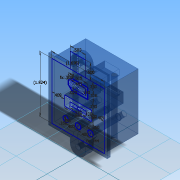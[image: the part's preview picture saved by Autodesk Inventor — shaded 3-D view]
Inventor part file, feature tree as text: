
AUTODESK INVENTOR PART (.ipt)
format: ipt  version: 2014 SP2 (Build 180246200, 246)  size: 236,544 bytes
history: native  units: in
note: dims shown in document units (in); Inventor stores cm internally (conversion verified against a paired STEP export)
features: extrude x10, sketch x4, hole x2, fillet x2, mirror x2, plane x1, projected_geometry x1
ambient origin geometry x8: Origin, YZ Plane, XZ Plane, XY Plane, X Axis, Y Axis, Z Axis, Center Point
bodies: Solid1 (feature_tree)
feature tree (22):
  sketch  "Sketch1"  dims[d1=0.316in d6=0.465in d7=0.19in]
  extrude  "Base"  Depth=0.465in
  extrude  "Flange"  Depth=0.25in
  sketch  "Sketch4"  dims[d19=0.4088in d20=0.4088in d21=1.1in d22=0.0in d23=0.91in d24=0.0in d25=0.16in d26=0.81in d27=0.0in d28=1.03in d29=0.0in d30=1.03in d31=0.0in d32=0.724in d33=0.0in d34=1.03in d35=0.0in d36=0.605in d37=0.25in d38=0.25in d39=0.1in d40=0.1in d42=0.02in d43=0.418in d44=0.0in d45=0.55in d46=0.63in d47=0.15in d48=0.75in d49=0.279in d50=0.25in d51=0.5635in d52=1.0in d53=0.8108in d54=0.1in d55=0.1in d56=0.0in d57=0.5in d58=0.5in d59=0.25in d60=0.0in d61=0.15in d62=0.75in d63=0.279in d64=0.25in d65=0.5635in d66=1.0in d67=0.8108in d68=0.25in d70=0.125in d71=1.6975in d72=1.8235in]
  extrude  "Mounting Tab"  Depth=0.25in
  hole  "Mounting Hole"  [1 undecoded]
  fillet  "Fillet1"  Radius=1.1in
  plane  "Work Plane1"
  mirror  "Mirror3"
  fillet  "Fillet2"  Radius=0.91in
  extrude  "Bullet"  Depth=1.8235in
  extrude  "Bullet Wire"  Depth=0.81in TaperAngle=0.0deg
  extrude  "Balance"  Depth=1.03in TaperAngle=0.0deg
  extrude  "Balance Wire"  Depth=1.03in TaperAngle=0.0deg
  extrude  "XT60 Holder"  Depth=0.724in TaperAngle=0.0deg
  extrude  "XT60 Wire"  Depth=1.03in TaperAngle=0.0deg
  extrude  "XT60 Shroud Space"  Depth=0.605in
  hole  "Hole1"  [1 undecoded]
  mirror  "Mirror1"
  sketch  "Sketch2"  dims[d8=0.88in d9=0.32in d10=0.52in d11=0.1in d12=0.1875in d13=0.4in d14=0.4in d15=0.25in]
  sketch  "Sketch3"  dims[d16=0.25in d17=0.25in d18=0.3438in]
  projected_geometry  "Projected Loop1"
note: 2 required parameter values undecoded (feature->parameter linkage not recoverable at this tier; creation-order binding heuristic only, values carry confidence <= 0.55)
